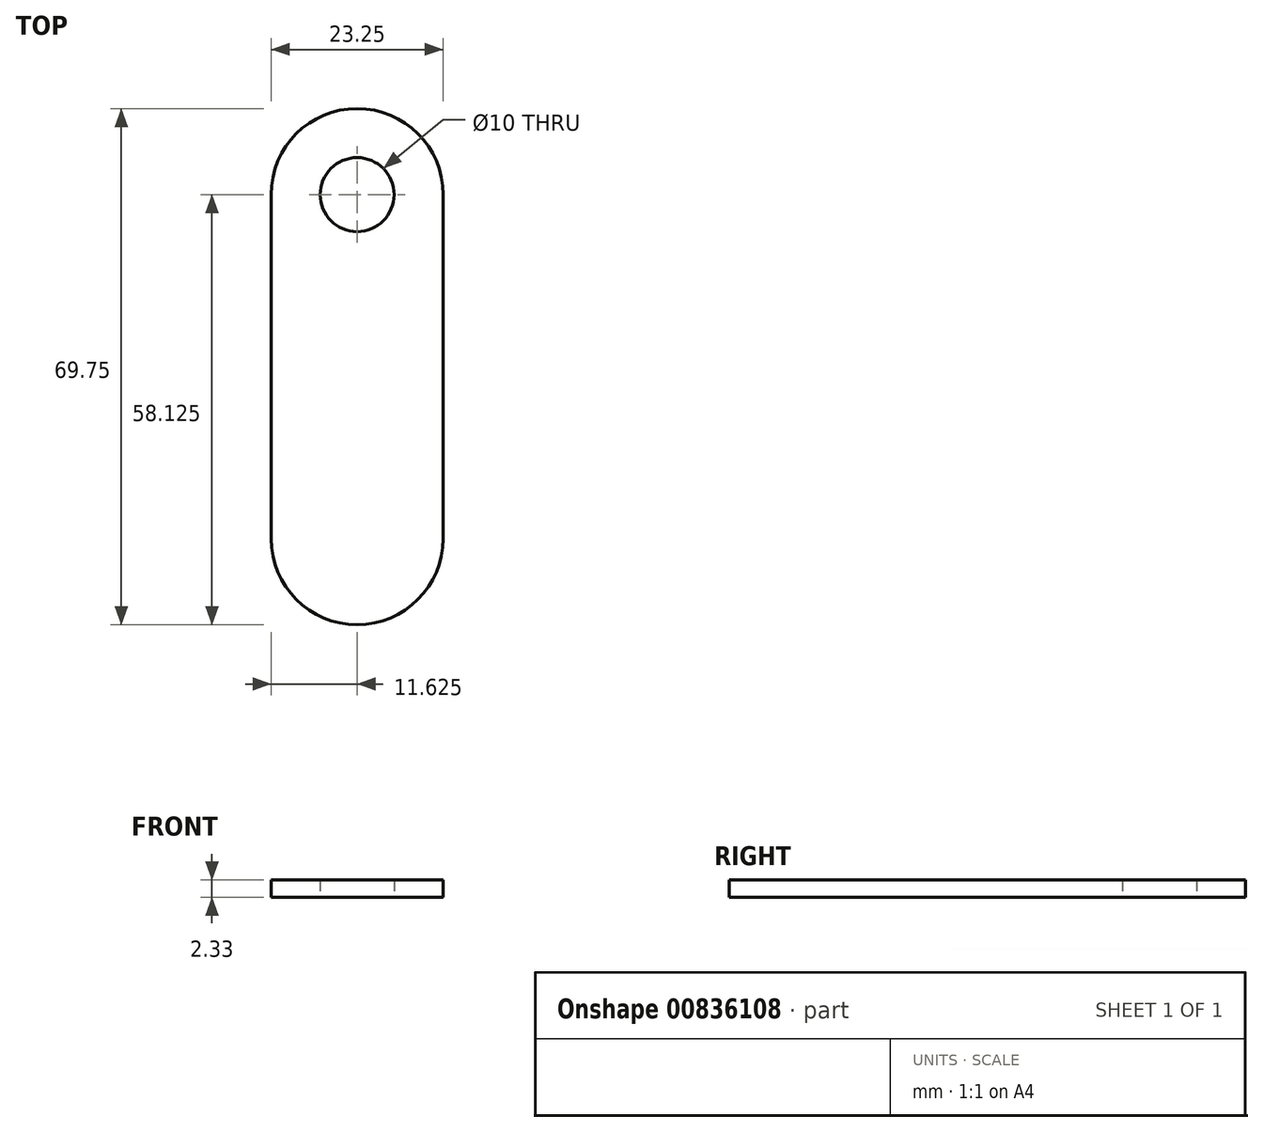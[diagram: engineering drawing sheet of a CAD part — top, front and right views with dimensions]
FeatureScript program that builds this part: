
annotation { "Feature Type Name" : "Feature", "Feature Type Description" : "" }
export const myFeature = defineFeature(function(context is Context, id is Id, definition is map)
    precondition{}
    {
        {
            var Q0;
            Q0=qCreatedBy(makeId("Top.planeOp"),FACE);
            var sketch = newSketch(context, id + "F0", { "sketchPlane" : qUnion([Q0])});
            skLineSegment(sketch, "E0.bottom", {"start": v(0, 69.75) * mm, "end": v(23.25, 69.75) * mm});
            skLineSegment(sketch, "E0.top", {"start": v(0, 0) * mm, "end": v(23.25, 0) * mm});
            skLineSegment(sketch, "E0.left", {"start": v(0, 69.75) * mm, "end": v(0, 0) * mm});
            skLineSegment(sketch, "E0.right", {"start": v(23.25, 69.75) * mm, "end": v(23.25, 0) * mm});
            skPoint(sketch, "E1", {"position": v(11.62, 58.13) * mm});
            skPoint(sketch, "E1.positionSnap0", {"position": v(11.62, 69.75) * mm});
            skCircle(sketch, "E2", {"center": v(11.62, 58.13) * mm, "radius": 5 * mm});
            skSolve(sketch);
        }
        {
            var Q0;
            Q0=makeQuery(id+"F0.imprint","IMPRINT",FACE,{"disambiguationData":[TD([[makeQuery(id+"F0.imprint","IMPRINT",EDGE,{"derivedFrom":sQuery(id+"F0.wireOp",EDGE,"E0.bottom")}),-1.0]])]});
            extrude(context, id + "F1", {"entities" : qUnion([Q0]), "depth" : 2.33 * mm, "offsetDistance" : 25 * mm});
        }
        {
            var Q0;
            Q0=makeQuery(id+"F1.opExtrude","SWEPT_EDGE",EDGE,{"disambiguationData":[OSD([sQuery(id+"F0.wireOp",EDGE,"E0.top"),sQuery(id+"F0.wireOp",EDGE,"E0.right")])]});
            var Q1;
            Q1=makeQuery(id+"F1.opExtrude","SWEPT_EDGE",EDGE,{"disambiguationData":[OSD([sQuery(id+"F0.wireOp",EDGE,"E0.top"),sQuery(id+"F0.wireOp",EDGE,"E0.left")])]});
            var Q2;
            Q2=makeQuery(id+"F1.opExtrude","SWEPT_EDGE",EDGE,{"disambiguationData":[OSD([sQuery(id+"F0.wireOp",EDGE,"E0.bottom"),sQuery(id+"F0.wireOp",EDGE,"E0.left")])]});
            var Q3;
            Q3=makeQuery(id+"F1.opExtrude","SWEPT_EDGE",EDGE,{"disambiguationData":[OSD([sQuery(id+"F0.wireOp",EDGE,"E0.bottom"),sQuery(id+"F0.wireOp",EDGE,"E0.right")])]});
            fillet(context, id + "F2", {"entities" : qUnion([Q0, Q1, Q2, Q3]), "radius" : (23.25 / 2) * mm, "tangentPropagation" : true, "allowEdgeOverflow" : false});
        }
    });
